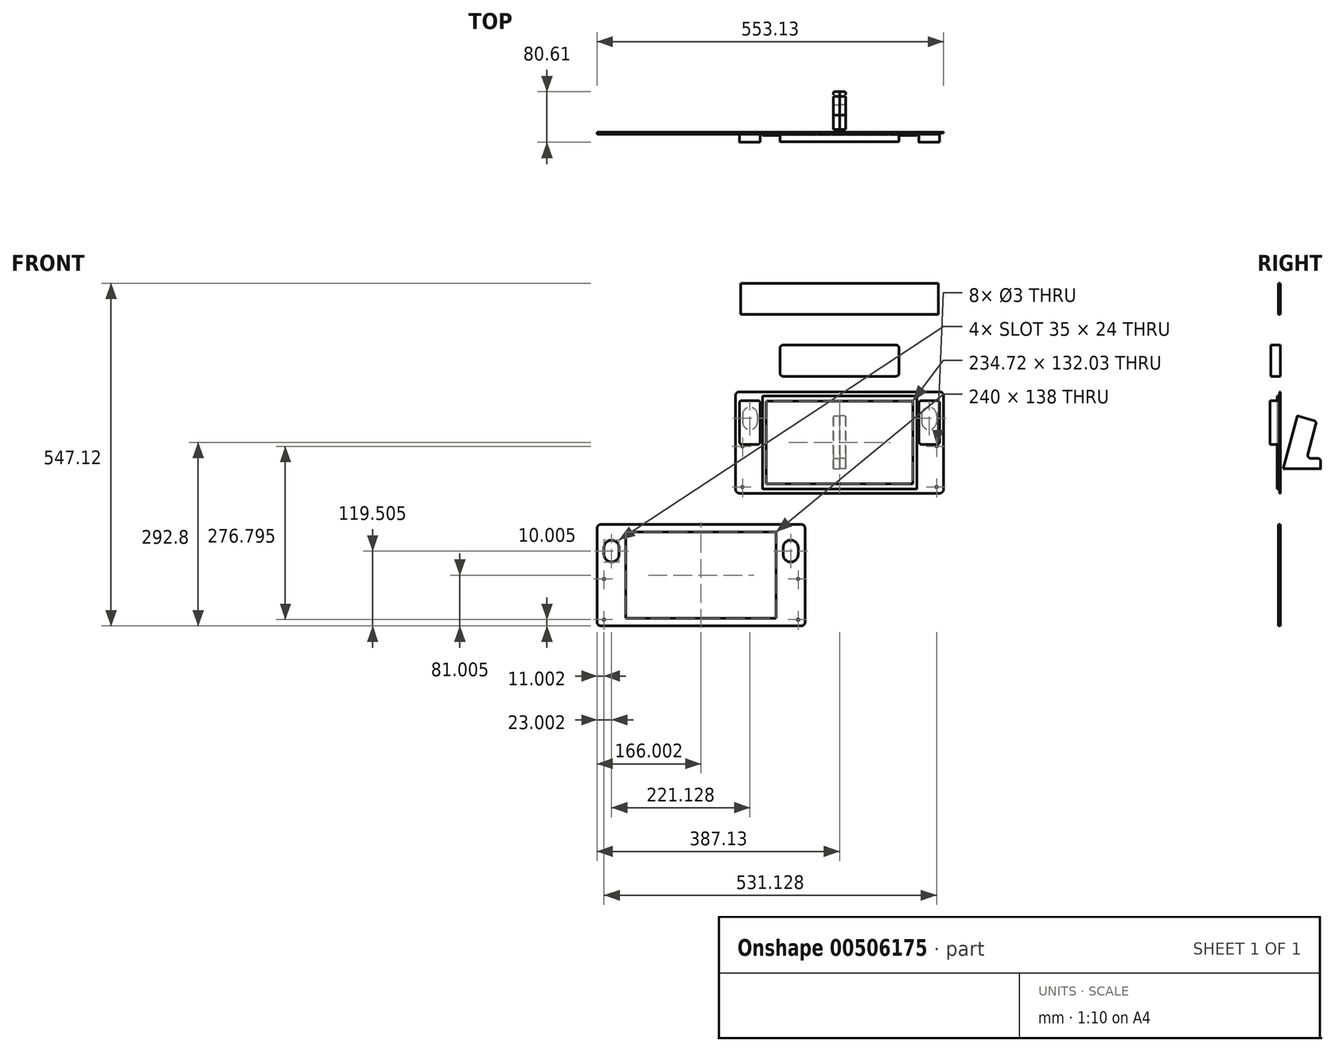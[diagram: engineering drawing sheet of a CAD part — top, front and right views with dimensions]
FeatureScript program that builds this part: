
annotation { "Feature Type Name" : "Feature", "Feature Type Description" : "" }
export const myFeature = defineFeature(function(context is Context, id is Id, definition is map)
    precondition{}
    {
        {
            var Q0;
            Q0=qCreatedBy(makeId("Front.planeOp"),FACE);
            var sketch = newSketch(context, id + "F0", { "sketchPlane" : qUnion([Q0])});
            skLineSegment(sketch, "E0.bottom", {"start": v(123.26, 74.51) * mm, "end": v(-123.26, 74.5) * mm});
            skLineSegment(sketch, "E0.top", {"start": v(123.26, -74.5) * mm, "end": v(-123.26, -74.51) * mm});
            skLineSegment(sketch, "E0.left", {"start": v(123.26, 74.51) * mm, "end": v(123.26, -74.5) * mm});
            skLineSegment(sketch, "E0.right", {"start": v(-123.26, 74.5) * mm, "end": v(-123.26, -74.51) * mm});
            skPoint(sketch, "E0.middle", {"position": v(0, 0) * mm});
            skLineSegment(sketch, "E1.bottom", {"start": v(117.36, 66.02) * mm, "end": v(-117.36, 66.02) * mm});
            skLineSegment(sketch, "E1.top", {"start": v(117.36, -66.02) * mm, "end": v(-117.36, -66.02) * mm});
            skLineSegment(sketch, "E1.left", {"start": v(117.36, 66.02) * mm, "end": v(117.36, -66.01) * mm});
            skLineSegment(sketch, "E1.right", {"start": v(-117.36, 66.02) * mm, "end": v(-117.36, -66.02) * mm});
            skSolve(sketch);
        }
        {
            var Q0;
            Q0=qCreatedBy(makeId("Front.planeOp"),FACE);
            var sketch = newSketch(context, id + "F1", { "sketchPlane" : qUnion([Q0])});
            skLineSegment(sketch, "E2.bottom", {"start": v(160, -81) * mm, "end": v(-160, -81) * mm});
            skLineSegment(sketch, "E2.top", {"start": v(160, 81) * mm, "end": v(-160, 81) * mm});
            skLineSegment(sketch, "E2.left", {"start": v(166, -75) * mm, "end": v(166, 75) * mm});
            skLineSegment(sketch, "E2.right", {"start": v(-166, -75) * mm, "end": v(-166, 75) * mm});
            skPoint(sketch, "E2.middle", {"position": v(0, 0) * mm});
            skPoint(sketch, "E3.visualSharp", {"position": v(-166, -81) * mm});
            skArc(sketch, "E3.filletArc", {"start": v(-166, -75) * mm, "mid": v(-164.24, -79.24) * mm, "end": v(-160, -81) * mm});
            skPoint(sketch, "E4.visualSharp", {"position": v(166, -81) * mm});
            skArc(sketch, "E4.filletArc", {"start": v(160, -81) * mm, "mid": v(164.24, -79.24) * mm, "end": v(166, -75) * mm});
            skPoint(sketch, "E5.visualSharp", {"position": v(166, 81) * mm});
            skArc(sketch, "E5.filletArc", {"start": v(166, 75) * mm, "mid": v(164.24, 79.24) * mm, "end": v(160, 81) * mm});
            skPoint(sketch, "E6.visualSharp", {"position": v(-166, 81) * mm});
            skArc(sketch, "E6.filletArc", {"start": v(-160, 81) * mm, "mid": v(-164.24, 79.24) * mm, "end": v(-166, 75) * mm});
            skLineSegment(sketch, "E7.bottom", {"start": v(143, 56) * mm, "end": v(143, 56) * mm});
            skLineSegment(sketch, "E7.top", {"start": v(143, 21) * mm, "end": v(143, 21) * mm});
            skLineSegment(sketch, "E7.left", {"start": v(131, 44) * mm, "end": v(131, 33) * mm});
            skLineSegment(sketch, "E7.right", {"start": v(155, 44) * mm, "end": v(155, 33) * mm});
            skPoint(sketch, "E8.visualSharp", {"position": v(131, 56) * mm});
            skArc(sketch, "E8.filletArc", {"start": v(143, 56) * mm, "mid": v(134.51, 52.49) * mm, "end": v(131, 44) * mm});
            skPoint(sketch, "E9.visualSharp", {"position": v(155, 56) * mm});
            skArc(sketch, "E9.filletArc", {"start": v(155, 44) * mm, "mid": v(151.49, 52.49) * mm, "end": v(143, 56) * mm});
            skPoint(sketch, "E10.visualSharp", {"position": v(155, 21) * mm});
            skArc(sketch, "E10.filletArc", {"start": v(143, 21) * mm, "mid": v(151.49, 24.51) * mm, "end": v(155, 33) * mm});
            skPoint(sketch, "E11.visualSharp", {"position": v(131, 21) * mm});
            skArc(sketch, "E11.filletArc", {"start": v(131, 33) * mm, "mid": v(134.51, 24.51) * mm, "end": v(143, 21) * mm});
            skLineSegment(sketch, "E12.bottom", {"start": v(-143, 56) * mm, "end": v(-143, 56) * mm});
            skLineSegment(sketch, "E12.top", {"start": v(-143, 21) * mm, "end": v(-143, 21) * mm});
            skLineSegment(sketch, "E12.left", {"start": v(-155, 44) * mm, "end": v(-155, 33) * mm});
            skLineSegment(sketch, "E12.right", {"start": v(-131, 44) * mm, "end": v(-131, 33) * mm});
            skPoint(sketch, "E13.visualSharp", {"position": v(-131, 56) * mm});
            skArc(sketch, "E13.filletArc", {"start": v(-131, 44) * mm, "mid": v(-134.51, 52.49) * mm, "end": v(-143, 56) * mm});
            skPoint(sketch, "E14.visualSharp", {"position": v(-155, 56) * mm});
            skArc(sketch, "E14.filletArc", {"start": v(-143, 56) * mm, "mid": v(-151.49, 52.49) * mm, "end": v(-155, 44) * mm});
            skPoint(sketch, "E15.visualSharp", {"position": v(-155, 21) * mm});
            skArc(sketch, "E15.filletArc", {"start": v(-155, 33) * mm, "mid": v(-151.49, 24.51) * mm, "end": v(-143, 21) * mm});
            skPoint(sketch, "E16.visualSharp", {"position": v(-131, 21) * mm});
            skArc(sketch, "E16.filletArc", {"start": v(-143, 21) * mm, "mid": v(-134.51, 24.51) * mm, "end": v(-131, 33) * mm});
            skCircle(sketch, "E17", {"center": v(155, -71) * mm, "radius": 1.5 * mm});
            skCircle(sketch, "E18", {"center": v(155, -6) * mm, "radius": 1.5 * mm});
            skCircle(sketch, "E19", {"center": v(-155, -71) * mm, "radius": 1.5 * mm});
            skCircle(sketch, "E20", {"center": v(-155, -6) * mm, "radius": 1.5 * mm});
            skSolve(sketch);
        }
        {
            var Q0;
            Q0=qCreatedBy(makeId("Front.planeOp"),FACE);
            var sketch = newSketch(context, id + "F2", { "sketchPlane" : qUnion([Q0])});
            skLineSegment(sketch, "E21.bottom", {"start": v(-155.76, 67) * mm, "end": v(-130.76, 67) * mm});
            skLineSegment(sketch, "E21.top", {"start": v(-155.76, -3) * mm, "end": v(-130.76, -3) * mm});
            skLineSegment(sketch, "E21.left", {"start": v(-159.76, 63) * mm, "end": v(-159.76, 1) * mm});
            skLineSegment(sketch, "E21.right", {"start": v(-126.76, 63) * mm, "end": v(-126.76, 1) * mm});
            skPoint(sketch, "E22.visualSharp", {"position": v(-159.76, 67) * mm});
            skArc(sketch, "E22.filletArc", {"start": v(-155.76, 67) * mm, "mid": v(-158.59, 65.84) * mm, "end": v(-159.76, 63) * mm});
            skPoint(sketch, "E23.visualSharp", {"position": v(154.5, 63.03) * mm});
            skArc(sketch, "E23.filletArc", {"start": v(-126.76, 63) * mm, "mid": v(-127.93, 65.84) * mm, "end": v(-130.76, 67.01) * mm});
            skPoint(sketch, "E24.visualSharp", {"position": v(-126.76, -3) * mm});
            skArc(sketch, "E24.filletArc", {"start": v(-130.76, -3) * mm, "mid": v(-127.93, -1.82) * mm, "end": v(-126.76, 1) * mm});
            skPoint(sketch, "E25.visualSharp", {"position": v(-159.76, -3) * mm});
            skArc(sketch, "E25.filletArc", {"start": v(-159.76, 1) * mm, "mid": v(-158.59, -1.82) * mm, "end": v(-155.76, -3) * mm});
            skLineSegment(sketch, "E26.bottom", {"start": v(130.76, 67.01) * mm, "end": v(155.76, 67.01) * mm});
            skLineSegment(sketch, "E26.top", {"start": v(130.76, -3) * mm, "end": v(155.76, -3) * mm});
            skLineSegment(sketch, "E26.left", {"start": v(126.76, 63) * mm, "end": v(126.76, 1) * mm});
            skLineSegment(sketch, "E26.right", {"start": v(159.76, 63) * mm, "end": v(159.76, 1) * mm});
            skPoint(sketch, "E27.visualSharp", {"position": v(126.76, 67.01) * mm});
            skArc(sketch, "E27.filletArc", {"start": v(130.76, 67.01) * mm, "mid": v(127.93, 65.84) * mm, "end": v(126.76, 63) * mm});
            skPoint(sketch, "E28.visualSharp", {"position": v(159.76, 67.01) * mm});
            skArc(sketch, "E28.filletArc", {"start": v(159.76, 63) * mm, "mid": v(158.59, 65.84) * mm, "end": v(155.76, 67.01) * mm});
            skPoint(sketch, "E29.visualSharp", {"position": v(159.76, -3) * mm});
            skArc(sketch, "E29.filletArc", {"start": v(155.76, -3) * mm, "mid": v(158.59, -1.82) * mm, "end": v(159.76, 1) * mm});
            skPoint(sketch, "E30.visualSharp", {"position": v(126.76, -3) * mm});
            skArc(sketch, "E30.filletArc", {"start": v(126.76, 1) * mm, "mid": v(127.93, -1.82) * mm, "end": v(130.76, -3) * mm});
            skSolve(sketch);
        }
        {
            var Q0;
            Q0=qCreatedBy(makeId("Front.planeOp"),FACE);
            var sketch = newSketch(context, id + "F3", { "sketchPlane" : qUnion([Q0])});
            skLineSegment(sketch, "E31.bottom", {"start": v(-95, 110.7) * mm, "end": v(-95, 150.7) * mm});
            skLineSegment(sketch, "E31.top", {"start": v(95, 110.7) * mm, "end": v(95, 150.7) * mm});
            skLineSegment(sketch, "E31.left", {"start": v(-90, 105.7) * mm, "end": v(90, 105.7) * mm});
            skLineSegment(sketch, "E31.right", {"start": v(-90, 155.7) * mm, "end": v(90, 155.7) * mm});
            skPoint(sketch, "E32.visualSharp", {"position": v(-95, 155.7) * mm});
            skArc(sketch, "E32.filletArc", {"start": v(-90, 155.7) * mm, "mid": v(-93.54, 154.23) * mm, "end": v(-95, 150.7) * mm});
            skPoint(sketch, "E33.visualSharp", {"position": v(-95, 105.7) * mm});
            skArc(sketch, "E33.filletArc", {"start": v(-95, 110.7) * mm, "mid": v(-93.54, 107.16) * mm, "end": v(-90, 105.7) * mm});
            skPoint(sketch, "E34.visualSharp", {"position": v(95, 105.7) * mm});
            skArc(sketch, "E34.filletArc", {"start": v(90, 105.7) * mm, "mid": v(93.54, 107.16) * mm, "end": v(95, 110.7) * mm});
            skPoint(sketch, "E35.visualSharp", {"position": v(95, 155.7) * mm});
            skArc(sketch, "E35.filletArc", {"start": v(95, 150.7) * mm, "mid": v(93.54, 154.23) * mm, "end": v(90, 155.7) * mm});
            skSolve(sketch);
        }
        {
            var Q0;
            Q0=qCreatedBy(makeId("Right.planeOp"),FACE);
            var sketch = newSketch(context, id + "F4", { "sketchPlane" : qUnion([Q0])});
            skLineSegment(sketch, "E36", {"start": v(27.23, 42.32) * mm, "end": v(4.6, -42.1) * mm});
            skLineSegment(sketch, "E37", {"start": v(4.6, -42.1) * mm, "end": v(64.6, -42.1) * mm});
            skLineSegment(sketch, "E38", {"start": v(64.6, -42.1) * mm, "end": v(64.6, -30.41) * mm});
            skLineSegment(sketch, "E39", {"start": v(59.6, -25.41) * mm, "end": v(48.85, -25.41) * mm});
            skLineSegment(sketch, "E40", {"start": v(44.03, -19.12) * mm, "end": v(56.97, 29.18) * mm});
            skLineSegment(sketch, "E41", {"start": v(53.43, 35.3) * mm, "end": v(27.23, 42.32) * mm});
            skPoint(sketch, "E42.visualSharp", {"position": v(58.26, 34) * mm});
            skArc(sketch, "E42.filletArc", {"start": v(56.97, 29.18) * mm, "mid": v(56.47, 32.97) * mm, "end": v(53.43, 35.3) * mm});
            skPoint(sketch, "E43.visualSharp", {"position": v(42.34, -25.41) * mm});
            skArc(sketch, "E43.filletArc", {"start": v(44.03, -19.12) * mm, "mid": v(44.89, -23.46) * mm, "end": v(48.85, -25.41) * mm});
            skPoint(sketch, "E44.visualSharp", {"position": v(64.6, -25.41) * mm});
            skArc(sketch, "E44.filletArc", {"start": v(64.6, -30.41) * mm, "mid": v(63.14, -26.88) * mm, "end": v(59.6, -25.41) * mm});
            skSolve(sketch);
        }
        {
            var Q0;
            Q0 = qSketchRegion(id + "F4", true);
            extrude(context, id + "F5", {"entities" : qUnion([Q0]), "depth" : 10 * mm});
        }
        {
            var Q0;
            Q0=makeQuery(id+"F5.opExtrude","CAP_EDGE",EDGE,{"disambiguationData":[OSD([sQuery(id+"F4.wireOp",EDGE,"E41")])],"isStart":false});
            fillet(context, id + "F6", {"entities" : qUnion([Q0]), "radius" : 2 * mm, "tangentPropagation" : true, "allowEdgeOverflow" : false});
        }
        {
            var Q0;
            Q0 = qSketchRegion(id + "F2", true);
            extrude(context, id + "F7", {"entities" : qUnion([Q0]), "depth" : 16 * mm});
        }
        {
            var Q0;
            Q0 = qSketchRegion(id + "F1", true);
            extrude(context, id + "F8", {"entities" : qUnion([Q0]), "depth" : 1 * mm});
        }
        {
            var Q0;
            Q0 = qSketchRegion(id + "F0", true);
            extrude(context, id + "F9", {"entities" : qUnion([Q0]), "depth" : 5.2 * mm});
        }
        {
            var Q0;
            Q0=makeQuery(id+"F5.opExtrude","SWEPT_BODY",BODY,{"disambiguationData":[OSD([sQuery(id+"F4.wireOp",EDGE,"E36"),sQuery(id+"F4.wireOp",EDGE,"E37"),sQuery(id+"F4.wireOp",EDGE,"E38"),sQuery(id+"F4.wireOp",EDGE,"E39"),sQuery(id+"F4.wireOp",EDGE,"E40"),sQuery(id+"F4.wireOp",EDGE,"E41"),sQuery(id+"F4.wireOp",EDGE,"E42.filletArc"),sQuery(id+"F4.wireOp",EDGE,"E43.filletArc"),sQuery(id+"F4.wireOp",EDGE,"E44.filletArc")])]});
            var Q1;
            Q1=qCreatedBy(makeId("Right.planeOp"),FACE);
            mirror(context, id + "F10", {"entities" : qUnion([Q0]), "mirrorPlane" : qUnion([Q1])});
        }
        {
            var Q0;
            Q0 = qSketchRegion(id + "F3", true);
            extrude(context, id + "F11", {"entities" : qUnion([Q0]), "depth" : 15 * mm});
        }
        {
            var Q0;
            Q0=qCreatedBy(makeId("Front.planeOp"),FACE);
            var sketch = newSketch(context, id + "F12", { "sketchPlane" : qUnion([Q0])});
            skLineSegment(sketch, "E45.bottom", {"start": v(158, 254.32) * mm, "end": v(-158, 254.32) * mm});
            skLineSegment(sketch, "E45.top", {"start": v(158, 204.32) * mm, "end": v(-158, 204.32) * mm});
            skLineSegment(sketch, "E45.left", {"start": v(158, 254.32) * mm, "end": v(158, 204.32) * mm});
            skLineSegment(sketch, "E45.right", {"start": v(-158, 254.32) * mm, "end": v(-158, 204.32) * mm});
            skPoint(sketch, "E45.middle", {"position": v(0, 229.32) * mm});
            skSolve(sketch);
        }
        {
            var Q0;
            Q0 = qSketchRegion(id + "F12", true);
            extrude(context, id + "F13", {"entities" : qUnion([Q0]), "depth" : 3 * mm});
        }
        {
            var Q0;
            Q0=qCreatedBy(makeId("Front.planeOp"),FACE);
            var sketch = newSketch(context, id + "F14", { "sketchPlane" : qUnion([Q0])});
            skLineSegment(sketch, "E46.bottom", {"start": v(-101.13, -280.8) * mm, "end": v(-341.13, -280.8) * mm});
            skLineSegment(sketch, "E46.top", {"start": v(-101.13, -142.8) * mm, "end": v(-341.13, -142.8) * mm});
            skLineSegment(sketch, "E46.left", {"start": v(-101.13, -280.8) * mm, "end": v(-101.13, -142.8) * mm});
            skLineSegment(sketch, "E46.right", {"start": v(-341.13, -280.8) * mm, "end": v(-341.13, -142.8) * mm});
            skPoint(sketch, "E46.middle", {"position": v(-221.13, -211.8) * mm});
            skLineSegment(sketch, "E47.bottom", {"start": v(-61.13, -292.8) * mm, "end": v(-381.13, -292.8) * mm});
            skLineSegment(sketch, "E47.top", {"start": v(-61.13, -130.8) * mm, "end": v(-381.13, -130.8) * mm});
            skLineSegment(sketch, "E47.left", {"start": v(-55.13, -286.8) * mm, "end": v(-55.13, -136.8) * mm});
            skLineSegment(sketch, "E47.right", {"start": v(-387.13, -286.8) * mm, "end": v(-387.13, -136.8) * mm});
            skPoint(sketch, "E48.visualSharp", {"position": v(-387.13, -130.8) * mm});
            skArc(sketch, "E48.filletArc", {"start": v(-381.13, -130.8) * mm, "mid": v(-385.37, -132.55) * mm, "end": v(-387.13, -136.8) * mm});
            skPoint(sketch, "E49.visualSharp", {"position": v(-55.13, -130.8) * mm});
            skArc(sketch, "E49.filletArc", {"start": v(-55.13, -136.8) * mm, "mid": v(-56.89, -132.55) * mm, "end": v(-61.13, -130.8) * mm});
            skPoint(sketch, "E50.visualSharp", {"position": v(-55.13, -292.8) * mm});
            skArc(sketch, "E50.filletArc", {"start": v(-61.13, -292.8) * mm, "mid": v(-56.89, -291.04) * mm, "end": v(-55.13, -286.8) * mm});
            skPoint(sketch, "E51.visualSharp", {"position": v(-387.13, -292.8) * mm});
            skArc(sketch, "E51.filletArc", {"start": v(-387.13, -286.8) * mm, "mid": v(-385.37, -291.04) * mm, "end": v(-381.13, -292.8) * mm});
            skLineSegment(sketch, "E52.bottom", {"start": v(-78.13, -155.8) * mm, "end": v(-78.13, -155.8) * mm});
            skLineSegment(sketch, "E52.top", {"start": v(-78.13, -190.8) * mm, "end": v(-78.13, -190.8) * mm});
            skLineSegment(sketch, "E52.left", {"start": v(-90.13, -167.8) * mm, "end": v(-90.13, -178.8) * mm});
            skLineSegment(sketch, "E52.right", {"start": v(-66.13, -167.8) * mm, "end": v(-66.13, -178.8) * mm});
            skPoint(sketch, "E53.visualSharp", {"position": v(-66.13, -155.8) * mm});
            skArc(sketch, "E53.filletArc", {"start": v(-66.13, -167.8) * mm, "mid": v(-69.64, -159.3) * mm, "end": v(-78.13, -155.8) * mm});
            skPoint(sketch, "E54.visualSharp", {"position": v(-90.13, -155.8) * mm});
            skArc(sketch, "E54.filletArc", {"start": v(-78.13, -155.8) * mm, "mid": v(-86.61, -159.3) * mm, "end": v(-90.13, -167.8) * mm});
            skPoint(sketch, "E55.visualSharp", {"position": v(-66.13, -190.8) * mm});
            skArc(sketch, "E55.filletArc", {"start": v(-78.13, -190.8) * mm, "mid": v(-69.64, -187.28) * mm, "end": v(-66.13, -178.8) * mm});
            skPoint(sketch, "E56.visualSharp", {"position": v(-90.13, -190.8) * mm});
            skArc(sketch, "E56.filletArc", {"start": v(-90.13, -178.8) * mm, "mid": v(-86.61, -187.28) * mm, "end": v(-78.13, -190.8) * mm});
            skCircle(sketch, "E57", {"center": v(-66.13, -217.8) * mm, "radius": 1.5 * mm});
            skLineSegment(sketch, "E58.bottom", {"start": v(-364.13, -155.8) * mm, "end": v(-364.13, -155.8) * mm});
            skLineSegment(sketch, "E58.top", {"start": v(-364.13, -190.8) * mm, "end": v(-364.13, -190.8) * mm});
            skLineSegment(sketch, "E58.left", {"start": v(-376.13, -167.8) * mm, "end": v(-376.13, -178.8) * mm});
            skLineSegment(sketch, "E58.right", {"start": v(-352.13, -167.8) * mm, "end": v(-352.13, -178.8) * mm});
            skPoint(sketch, "E59.visualSharp", {"position": v(-376.13, -155.8) * mm});
            skArc(sketch, "E59.filletArc", {"start": v(-364.13, -155.8) * mm, "mid": v(-372.61, -159.3) * mm, "end": v(-376.13, -167.8) * mm});
            skPoint(sketch, "E60.visualSharp", {"position": v(-352.13, -155.8) * mm});
            skArc(sketch, "E60.filletArc", {"start": v(-352.13, -167.8) * mm, "mid": v(-355.64, -159.3) * mm, "end": v(-364.13, -155.8) * mm});
            skPoint(sketch, "E61.visualSharp", {"position": v(-352.13, -190.8) * mm});
            skArc(sketch, "E61.filletArc", {"start": v(-364.13, -190.8) * mm, "mid": v(-355.64, -187.28) * mm, "end": v(-352.13, -178.8) * mm});
            skPoint(sketch, "E62.visualSharp", {"position": v(-376.13, -190.8) * mm});
            skArc(sketch, "E62.filletArc", {"start": v(-376.13, -178.8) * mm, "mid": v(-372.61, -187.28) * mm, "end": v(-364.13, -190.8) * mm});
            skCircle(sketch, "E63", {"center": v(-66.13, -282.8) * mm, "radius": 1.5 * mm});
            skCircle(sketch, "E64", {"center": v(-376.13, -217.8) * mm, "radius": 1.5 * mm});
            skCircle(sketch, "E65", {"center": v(-376.13, -282.8) * mm, "radius": 1.5 * mm});
            skSolve(sketch);
        }
        {
            var Q0;
            Q0 = qSketchRegion(id + "F14", true);
            extrude(context, id + "F15", {"entities" : qUnion([Q0]), "depth" : 3 * mm});
        }
    });
